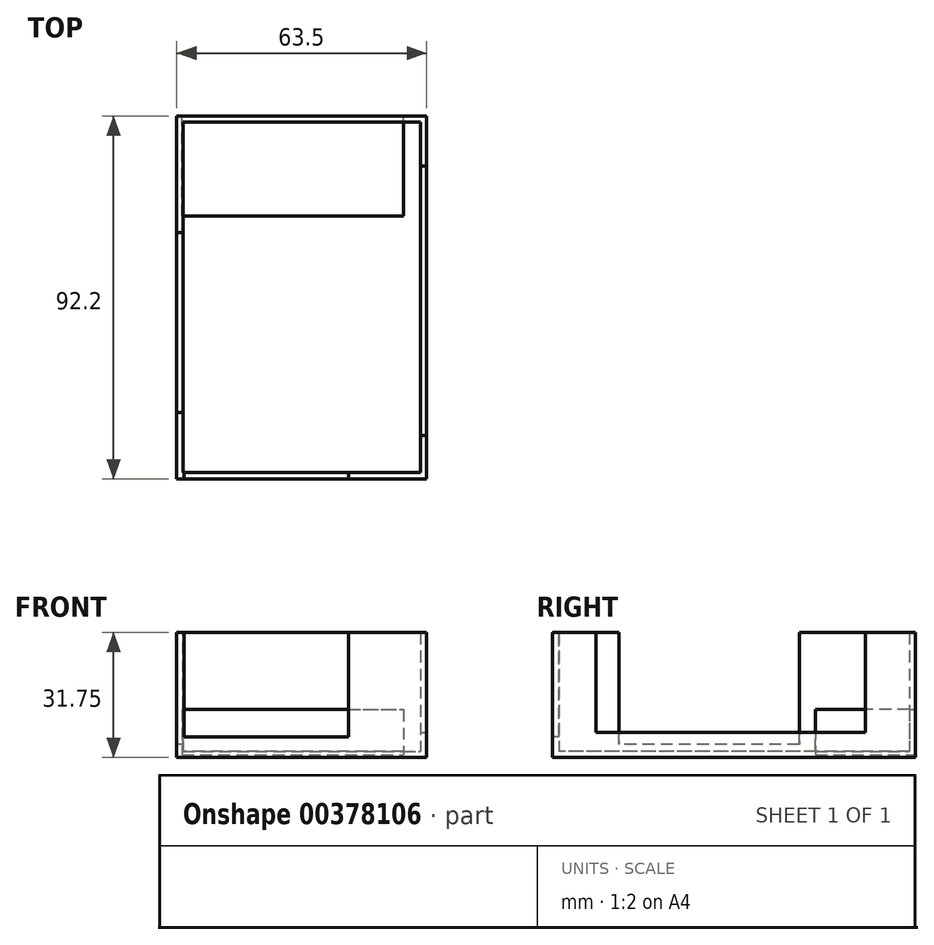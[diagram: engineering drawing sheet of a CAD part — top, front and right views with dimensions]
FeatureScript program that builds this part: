
annotation { "Feature Type Name" : "Feature", "Feature Type Description" : "" }
export const myFeature = defineFeature(function(context is Context, id is Id, definition is map)
    precondition{}
    {
        {
            var Q0;
            Q0=qCreatedBy(makeId("Top.planeOp"),FACE);
            var sketch = newSketch(context, id + "F0", { "sketchPlane" : qUnion([Q0])});
            skLineSegment(sketch, "E0.bottom", {"start": v(-29.39, 41.78) * mm, "end": v(34.11, 41.78) * mm});
            skLineSegment(sketch, "E0.top", {"start": v(-29.39, -50.42) * mm, "end": v(34.11, -50.42) * mm});
            skLineSegment(sketch, "E0.left", {"start": v(-29.39, 41.78) * mm, "end": v(-29.39, -50.42) * mm});
            skLineSegment(sketch, "E0.right", {"start": v(34.11, 41.78) * mm, "end": v(34.11, -50.42) * mm});
            skSolve(sketch);
        }
        {
            var Q0;
            Q0=makeQuery(id+"F0.imprint","IMPRINT",FACE,{"disambiguationData":[TD([[makeQuery(id+"F0.imprint","IMPRINT",EDGE,{"derivedFrom":sQuery(id+"F0.wireOp",EDGE,"E0.bottom")}),-1.0]])]});
            extrude(context, id + "F1", {"entities" : qUnion([Q0]), "depth" : 31.75 * mm});
        }
        {
            var Q0;
            Q0=makeQuery(id+"F1.opExtrude","CAP_FACE",FACE,{"disambiguationData":[OSD([sQuery(id+"F0.wireOp",EDGE,"E0.bottom"),sQuery(id+"F0.wireOp",EDGE,"E0.top"),sQuery(id+"F0.wireOp",EDGE,"E0.left"),sQuery(id+"F0.wireOp",EDGE,"E0.right")])],"isStart":false});
            shell(context, id + "F2", {"entities" : qUnion([Q0]), "thickness" : 1.59 * mm});
        }
        {
            var Q0;
            Q0=makeQuery(id+"F1.opExtrude","SWEPT_FACE",FACE,{"disambiguationData":[OSD([sQuery(id+"F0.wireOp",EDGE,"E0.right")])]});
            var sketch = newSketch(context, id + "F3", { "sketchPlane" : qUnion([Q0])});
            skLineSegment(sketch, "E1.bottom", {"start": v(-39.4, 31.75) * mm, "end": v(29.08, 31.75) * mm});
            skLineSegment(sketch, "E1.top", {"start": v(-39.4, 6.35) * mm, "end": v(29.08, 6.35) * mm});
            skLineSegment(sketch, "E1.left", {"start": v(-39.4, 31.75) * mm, "end": v(-39.4, 6.35) * mm});
            skLineSegment(sketch, "E1.right", {"start": v(29.08, 31.75) * mm, "end": v(29.08, 6.35) * mm});
            skSolve(sketch);
        }
        {
            var Q0;
            Q0 = qSketchRegion(id + "F3", true);
            extrude(context, id + "F4", {"entities" : qUnion([Q0]), "operationType" : NewBodyOperationType.REMOVE, "oppositeDirection" : true, "depth" : 25.4 * mm});
        }
        {
            var Q0;
            Q0=makeQuery(id+"F1.opExtrude","SWEPT_FACE",FACE,{"disambiguationData":[OSD([sQuery(id+"F0.wireOp",EDGE,"E0.top")])]});
            var sketch = newSketch(context, id + "F5", { "sketchPlane" : qUnion([Q0])});
            skLineSegment(sketch, "E2.bottom", {"start": v(-27.54, 31.75) * mm, "end": v(14.26, 31.75) * mm});
            skLineSegment(sketch, "E2.top", {"start": v(-27.54, 5.25) * mm, "end": v(14.26, 5.25) * mm});
            skLineSegment(sketch, "E2.left", {"start": v(-27.54, 31.75) * mm, "end": v(-27.54, 5.25) * mm});
            skLineSegment(sketch, "E2.right", {"start": v(14.26, 31.75) * mm, "end": v(14.26, 5.25) * mm});
            skSolve(sketch);
        }
        {
            var Q0;
            Q0 = qSketchRegion(id + "F5", true);
            extrude(context, id + "F6", {"entities" : qUnion([Q0]), "operationType" : NewBodyOperationType.REMOVE, "oppositeDirection" : true, "depth" : 25.4 * mm});
        }
        {
            var Q0;
            Q0=makeQuery(id+"F1.opExtrude","SWEPT_FACE",FACE,{"disambiguationData":[OSD([sQuery(id+"F0.wireOp",EDGE,"E0.left")])]});
            var sketch = newSketch(context, id + "F7", { "sketchPlane" : qUnion([Q0])});
            skLineSegment(sketch, "E3.bottom", {"start": v(-12.25, 31.75) * mm, "end": v(33.55, 31.75) * mm});
            skLineSegment(sketch, "E3.top", {"start": v(-12.25, 3.3) * mm, "end": v(33.55, 3.3) * mm});
            skLineSegment(sketch, "E3.left", {"start": v(-12.25, 31.75) * mm, "end": v(-12.25, 3.3) * mm});
            skLineSegment(sketch, "E3.right", {"start": v(33.55, 31.75) * mm, "end": v(33.55, 3.3) * mm});
            skSolve(sketch);
        }
        {
            var Q0;
            Q0 = qSketchRegion(id + "F7", true);
            extrude(context, id + "F8", {"entities" : qUnion([Q0]), "operationType" : NewBodyOperationType.REMOVE, "oppositeDirection" : true, "depth" : 25.4 * mm});
        }
        {
            var Q0;
            Q0=makeQuery(id+"F1.opExtrude","SWEPT_FACE",FACE,{"disambiguationData":[OSD([sQuery(id+"F0.wireOp",EDGE,"E0.bottom")])]});
            var sketch = newSketch(context, id + "F9", { "sketchPlane" : qUnion([Q0])});
            skLineSegment(sketch, "E4.bottom", {"start": v(28.03, 12.16) * mm, "end": v(-28.24, 12.16) * mm});
            skLineSegment(sketch, "E4.top", {"start": v(28.03, 0.62) * mm, "end": v(-28.24, 0.62) * mm});
            skLineSegment(sketch, "E4.left", {"start": v(28.03, 12.16) * mm, "end": v(28.03, 0.62) * mm});
            skLineSegment(sketch, "E4.right", {"start": v(-28.24, 12.16) * mm, "end": v(-28.24, 0.62) * mm});
            skSolve(sketch);
        }
        {
            var Q0;
            Q0 = qSketchRegion(id + "F9", true);
            extrude(context, id + "F10", {"entities" : qUnion([Q0]), "operationType" : NewBodyOperationType.REMOVE, "oppositeDirection" : true, "depth" : 25.4 * mm});
        }
    });
